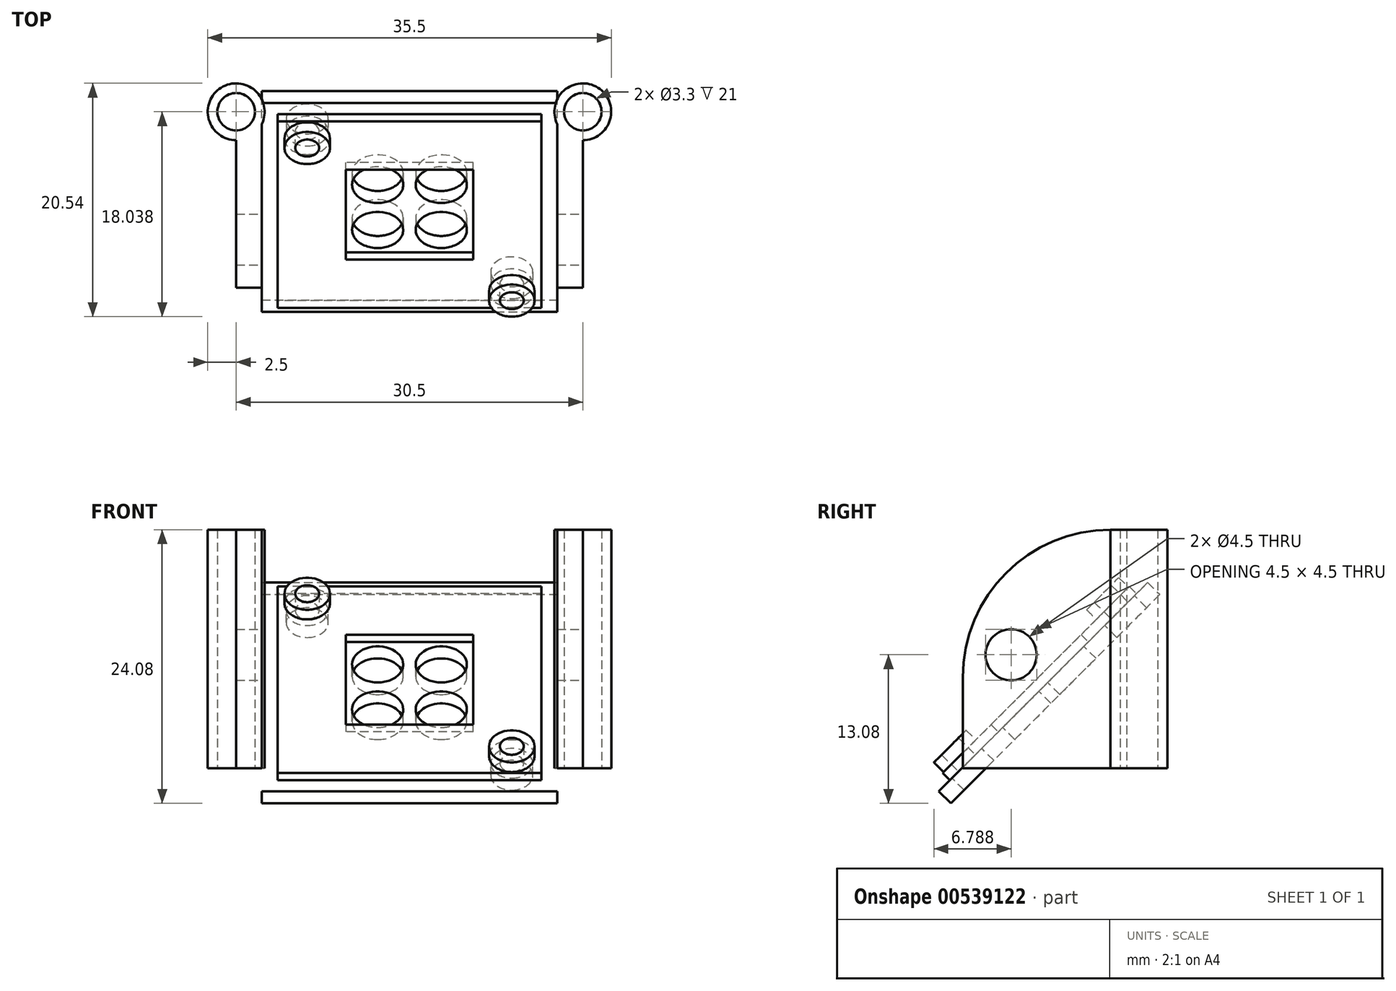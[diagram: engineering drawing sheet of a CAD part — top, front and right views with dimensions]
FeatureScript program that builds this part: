
annotation { "Feature Type Name" : "Feature", "Feature Type Description" : "" }
export const myFeature = defineFeature(function(context is Context, id is Id, definition is map)
    precondition{}
    {
        {
            var Q0;
            Q0=qCreatedBy(makeId("Top.planeOp"),FACE);
            var sketch = newSketch(context, id + "F0", { "sketchPlane" : qUnion([Q0])});
            skLineSegment(sketch, "E0", {"start": v(15.25, 24.62) * mm, "end": v(-15.25, 24.62) * mm, "construction": true});
            skCircle(sketch, "E1", {"center": v(-15.25, 24.62) * mm, "radius": 1.65 * mm});
            skCircle(sketch, "E2", {"center": v(-15.25, 24.62) * mm, "radius": 2.5 * mm});
            skCircle(sketch, "E3", {"center": v(15.25, 24.62) * mm, "radius": 1.65 * mm});
            skCircle(sketch, "E4", {"center": v(15.25, 24.62) * mm, "radius": 2.5 * mm});
            skPoint(sketch, "E5", {"position": v(-15.25, 22.12) * mm});
            skLineSegment(sketch, "E6", {"start": v(-15.25, 24.62) * mm, "end": v(-15.25, 9.12) * mm, "construction": true});
            skLineSegment(sketch, "E7", {"start": v(-15.25, 9.12) * mm, "end": v(15.25, 9.12) * mm, "construction": true});
            skLineSegment(sketch, "E8", {"start": v(15.25, 9.12) * mm, "end": v(15.25, 24.62) * mm, "construction": true});
            skLineSegment(sketch, "E9", {"start": v(15.25, 22.12) * mm, "end": v(15.25, 9.12) * mm});
            skLineSegment(sketch, "E10", {"start": v(15.25, 9.12) * mm, "end": v(13, 9.12) * mm});
            skLineSegment(sketch, "E11", {"start": v(13, 9.12) * mm, "end": v(13, 23.53) * mm});
            skLineSegment(sketch, "E12", {"start": v(-15.25, 22.12) * mm, "end": v(-15.25, 9.12) * mm});
            skLineSegment(sketch, "E13", {"start": v(-15.25, 9.12) * mm, "end": v(-13, 9.12) * mm});
            skLineSegment(sketch, "E14", {"start": v(-13, 9.12) * mm, "end": v(-13, 23.53) * mm});
            skSolve(sketch);
        }
        {
            var Q0;
            Q0=makeQuery(id+"F0.imprint","IMPRINT",FACE,{"disambiguationData":[TD([[makeQuery(id+"F0.imprint","IMPRINT",EDGE,{"derivedFrom":sQuery(id+"F0.wireOp",EDGE,"E1")}),-1.0]])]});
            var Q1;
            Q1=makeQuery(id+"F0.imprint","IMPRINT",FACE,{"disambiguationData":[TD([[makeQuery(id+"F0.imprint","IMPRINT",EDGE,{"derivedFrom":sQuery(id+"F0.wireOp",EDGE,"E3")}),-1.0]])]});
            var Q2;
            Q2=makeQuery(id+"F0.imprint","IMPRINT",FACE,{"disambiguationData":[TD([[makeQuery(id+"F0.imprint","IMPRINT",EDGE,{"derivedFrom":sQuery(id+"F0.wireOp",EDGE,"GyxC4Cwi-RMFc-qVmH-YboR-WA0SqB4U5H94")}),-1.0]])]});
            var Q3;
            Q3=makeQuery(id+"F0.imprint","IMPRINT",FACE,{"disambiguationData":[TD([[makeQuery(id+"F0.imprint","IMPRINT",EDGE,{"derivedFrom":sQuery(id+"F0.wireOp",EDGE,"82AeB47f-6y09-gEI0-IFZB-KstoD60AnrTl")}),-1.0]])]});
            var Q4;
            {var subQ0=sQuery(id+"F0.wireOp",EDGE,"E9");Q4=makeQuery(id+"F0.imprint","IMPRINT",FACE,{"disambiguationData":[TD([[makeQuery(id+"F0.imprint","IMPRINT",EDGE,{"derivedFrom":subQ0}),-1.0]])]});}
            var Q5;
            {var subQ0=sQuery(id+"F0.wireOp",EDGE,"E12");Q5=makeQuery(id+"F0.imprint","IMPRINT",FACE,{"disambiguationData":[TD([[makeQuery(id+"F0.imprint","IMPRINT",EDGE,{"derivedFrom":subQ0}),1.0]])]});}
            extrude(context, id + "F1", {"entities" : qUnion([Q0, Q1, Q2, Q3, Q4, Q5]), "depth" : 21 * mm, "offsetDistance" : 25 * mm});
        }
        {
            var Q0;
            Q0=makeQuery(id+"F1.opExtrude","CAP_EDGE",EDGE,{"disambiguationData":[OSD([sQuery(id+"F0.wireOp",EDGE,"E13")])],"isStart":false});
            var Q1;
            Q1=makeQuery(id+"F1.opExtrude","CAP_EDGE",EDGE,{"disambiguationData":[OSD([sQuery(id+"F0.wireOp",EDGE,"E10")])],"isStart":false});
            fillet(context, id + "F2", {"entities" : qUnion([Q0, Q1]), "radius" : 13 * mm, "tangentPropagation" : true, "allowEdgeOverflow" : false});
        }
        {
            var Q0;
            Q0=makeQuery(id+"F1.opExtrude","SWEPT_FACE",FACE,{"disambiguationData":[OSD([sQuery(id+"F0.wireOp",EDGE,"E9")])]});
            var sketch = newSketch(context, id + "F3", { "sketchPlane" : qUnion([Q0])});
            skLineSegment(sketch, "E15", {"start": v(9.12, 0) * mm, "end": v(13.37, 0) * mm, "construction": true});
            skLineSegment(sketch, "E16", {"start": v(13.37, 0) * mm, "end": v(13.37, 10) * mm, "construction": true});
            skCircle(sketch, "E17", {"center": v(13.37, 10) * mm, "radius": 2.25 * mm});
            skSolve(sketch);
        }
        {
            var Q0;
            Q0=sQuery(id+"F3.wireOp",VERTEX,"E17.center");
            var Q1;
            Q1=makeQuery(id+"F1.opExtrude","SWEPT_BODY",BODY,{"disambiguationData":[OSD([sQuery(id+"F0.wireOp",EDGE,"E1"),sQuery(id+"F0.wireOp",EDGE,"E2"),sQuery(id+"F0.wireOp",EDGE,"E12"),sQuery(id+"F0.wireOp",EDGE,"E13"),sQuery(id+"F0.wireOp",EDGE,"E14")])]});
            var Q2;
            Q2=makeQuery(id+"F1.opExtrude","SWEPT_BODY",BODY,{"disambiguationData":[OSD([sQuery(id+"F0.wireOp",EDGE,"E3"),sQuery(id+"F0.wireOp",EDGE,"E4"),sQuery(id+"F0.wireOp",EDGE,"E9"),sQuery(id+"F0.wireOp",EDGE,"E10"),sQuery(id+"F0.wireOp",EDGE,"E11")])]});
            hole(context, id + "F4", {"style" : HoleStyle.SIMPLE, "endStyle" : HoleEndStyle.THROUGH, "holeDiameter" : 4.5 * mm, "isTappedThrough" : true, "tappedDepth" : 12 * mm, "tapClearance" : 3, "locations" : qUnion([Q0]), "scope" : qUnion([Q1, Q2])});
        }
        {
            var Q0;
            Q0=makeQuery(id+"F1.opExtrude","SWEPT_FACE",FACE,{"disambiguationData":[OSD([sQuery(id+"F0.wireOp",EDGE,"E11")])]});
            var sketch = newSketch(context, id + "F5", { "sketchPlane" : qUnion([Q0])});
            skLineSegment(sketch, "E18", {"start": v(-13.37, 10) * mm, "end": v(-13.37, 0) * mm, "construction": true});
            skLineSegment(sketch, "E19", {"start": v(-13.37, 0) * mm, "end": v(-13.37, 10) * mm, "construction": true});
            skLineSegment(sketch, "E20", {"start": v(-13.37, 10) * mm, "end": v(-16.2, 7.17) * mm, "construction": true});
            skLineSegment(sketch, "E21", {"start": v(-16.2, 7.17) * mm, "end": v(-25.39, 16.36) * mm});
            skLineSegment(sketch, "E22", {"start": v(-25.39, 16.36) * mm, "end": v(-26.45, 15.3) * mm});
            skLineSegment(sketch, "E23", {"start": v(-26.45, 15.3) * mm, "end": v(-8.06, -3.08) * mm});
            skLineSegment(sketch, "E24", {"start": v(-8.06, -3.08) * mm, "end": v(-7, -2.02) * mm});
            skLineSegment(sketch, "E25", {"start": v(-7, -2.02) * mm, "end": v(-16.2, 7.17) * mm});
            skSolve(sketch);
        }
        {
            var Q0;
            {var subQ0=sQuery(id+"F5.wireOp",EDGE,"E25");var subQ1=sQuery(id+"F5.wireOp",EDGE,"E21");var subQ2=makeQuery(id+"F5.imprint","INTERSECT",VERTEX,{"derivedFrom":[subQ1,subQ0]});Q0=makeQuery(id+"F5.imprint","IMPRINT",FACE,{"disambiguationData":[TD([[makeQuery(id+"F5.imprint","IMPRINT",EDGE,{"disambiguationData":[TD([[subQ2,-1.0]])],"derivedFrom":subQ1}),1.0]])]});}
            var Q1;
            {var subQ0=sQuery(id+"F5.wireOp",EDGE,"E22");Q1=makeQuery(id+"F5.imprint","IMPRINT",FACE,{"disambiguationData":[TD([[makeQuery(id+"F5.imprint","IMPRINT",EDGE,{"derivedFrom":subQ0}),1.0]])]});}
            var Q2;
            {var subQ1=sQuery(id+"F5.wireOp",EDGE,"E24");Q2=makeQuery(id+"F5.imprint","IMPRINT",FACE,{"disambiguationData":[TD([[makeQuery(id+"F5.imprint","IMPRINT",EDGE,{"derivedFrom":subQ1}),1.0]])]});}
            extrude(context, id + "F6", {"entities" : qUnion([Q0, Q1, Q2]), "depth" : 26 * mm, "offsetDistance" : 25 * mm});
        }
        {
            var Q0;
            Q0=makeQuery(id+"F6.opExtrude","SWEPT_FACE",FACE,{"disambiguationData":[OSD([sQuery(id+"F5.wireOp",EDGE,"E21"),sQuery(id+"F5.wireOp",EDGE,"E25")])]});
            var sketch = newSketch(context, id + "F7", { "sketchPlane" : qUnion([Q0])});
            skLineSegment(sketch, "E26", {"start": v(-13, 29.52) * mm, "end": v(-9, 29.52) * mm, "construction": true});
            skLineSegment(sketch, "E27", {"start": v(-9, 29.52) * mm, "end": v(-9, 26.02) * mm, "construction": true});
            skLineSegment(sketch, "E28", {"start": v(13, 3.52) * mm, "end": v(9, 3.52) * mm, "construction": true});
            skLineSegment(sketch, "E29", {"start": v(9, 3.52) * mm, "end": v(9, 7.02) * mm, "construction": true});
            skPoint(sketch, "E30.endSnap0", {"position": v(0, 3.52) * mm});
            skLineSegment(sketch, "E31.bottom", {"start": v(11.6, 4.92) * mm, "end": v(-11.6, 4.92) * mm});
            skLineSegment(sketch, "E31.top", {"start": v(11.6, 28.12) * mm, "end": v(-11.6, 28.12) * mm});
            skLineSegment(sketch, "E31.left", {"start": v(11.6, 4.92) * mm, "end": v(11.6, 28.12) * mm});
            skLineSegment(sketch, "E31.right", {"start": v(-11.6, 4.92) * mm, "end": v(-11.6, 28.12) * mm});
            skPoint(sketch, "E31.middle", {"position": v(0, 16.52) * mm});
            skLineSegment(sketch, "E32.bottom", {"start": v(5.6, 10.92) * mm, "end": v(-5.6, 10.92) * mm});
            skLineSegment(sketch, "E32.top", {"start": v(5.6, 22.12) * mm, "end": v(-5.6, 22.12) * mm});
            skLineSegment(sketch, "E32.left", {"start": v(5.6, 10.92) * mm, "end": v(5.6, 22.12) * mm});
            skLineSegment(sketch, "E32.right", {"start": v(-5.6, 10.92) * mm, "end": v(-5.6, 22.12) * mm});
            skCircle(sketch, "E33", {"center": v(-9, 26.02) * mm, "radius": 1.05 * mm});
            skCircle(sketch, "E34", {"center": v(9, 7.02) * mm, "radius": 1.05 * mm});
            skCircle(sketch, "E35", {"center": v(9, 7.02) * mm, "radius": 2 * mm});
            skCircle(sketch, "E36", {"center": v(-9, 26.02) * mm, "radius": 2 * mm});
            skCircle(sketch, "E37", {"center": v(9, 7.02) * mm, "radius": 1.8 * mm, "construction": true});
            skCircle(sketch, "E38", {"center": v(-9, 26.02) * mm, "radius": 1.8 * mm, "construction": true});
            skLineSegment(sketch, "E39", {"start": v(0, 16.52) * mm, "end": v(-5.6, 16.52) * mm, "construction": true});
            skLineSegment(sketch, "E40", {"start": v(-2.8, 16.52) * mm, "end": v(-2.8, 22.12) * mm, "construction": true});
            skLineSegment(sketch, "E41", {"start": v(-2.8, 16.52) * mm, "end": v(-2.8, 10.92) * mm, "construction": true});
            skLineSegment(sketch, "E42", {"start": v(0, 16.52) * mm, "end": v(5.6, 16.52) * mm, "construction": true});
            skLineSegment(sketch, "E43", {"start": v(2.8, 16.52) * mm, "end": v(2.8, 22.12) * mm, "construction": true});
            skLineSegment(sketch, "E44", {"start": v(2.8, 16.52) * mm, "end": v(2.8, 10.92) * mm, "construction": true});
            skLineSegment(sketch, "E45", {"start": v(2.8, 13.72) * mm, "end": v(-2.8, 13.72) * mm, "construction": true});
            skLineSegment(sketch, "E46", {"start": v(-2.8, 13.72) * mm, "end": v(-2.8, 19.32) * mm, "construction": true});
            skLineSegment(sketch, "E47", {"start": v(-2.8, 19.32) * mm, "end": v(2.8, 19.32) * mm, "construction": true});
            skCircle(sketch, "E48", {"center": v(-2.8, 19.32) * mm, "radius": 2.25 * mm, "construction": true});
            skCircle(sketch, "E49", {"center": v(2.8, 19.32) * mm, "radius": 2.25 * mm, "construction": true});
            skCircle(sketch, "E50", {"center": v(2.8, 13.72) * mm, "radius": 2.25 * mm, "construction": true});
            skCircle(sketch, "E51", {"center": v(-2.8, 13.72) * mm, "radius": 2.25 * mm, "construction": true});
            skSolve(sketch);
        }
        {
            var Q0;
            Q0=sQuery(id+"F7.wireOp",VERTEX,"xRpNI7OB-sENC-NIWt-IonO-ULPQCYI2OJvv.center");
            var Q1;
            Q1=sQuery(id+"F7.wireOp",VERTEX,"aurLsu0g-ZDsF-CTWi-w7Pd-vwTeFcaxKEEF.center");
            var Q2;
            Q2=sQuery(id+"F7.wireOp",VERTEX,"E33.center");
            var Q3;
            Q3=sQuery(id+"F7.wireOp",VERTEX,"E29.end");
            var Q4;
            Q4=makeQuery(id+"F6.opExtrude","SWEPT_BODY",BODY,{"disambiguationData":[OSD([sQuery(id+"F5.wireOp",EDGE,"E21"),sQuery(id+"F5.wireOp",EDGE,"E22"),sQuery(id+"F5.wireOp",EDGE,"E23"),sQuery(id+"F5.wireOp",EDGE,"E24"),sQuery(id+"F5.wireOp",EDGE,"E25")])]});
            hole(context, id + "F8", {"style" : HoleStyle.SIMPLE, "endStyle" : HoleEndStyle.THROUGH, "holeDiameter" : 3.7 * mm, "isTappedThrough" : true, "tappedDepth" : 12 * mm, "tapClearance" : 3, "locations" : qUnion([Q0, Q1, Q2, Q3]), "scope" : qUnion([Q4])});
        }
        {
            var Q0;
            Q0=makeQuery(id+"F7.imprint","IMPRINT",FACE,{"disambiguationData":[TD([[makeQuery(id+"F7.imprint","IMPRINT",EDGE,{"derivedFrom":sQuery(id+"F7.wireOp",EDGE,"E31.bottom")}),-1.0]])]});
            extrude(context, id + "F9", {"entities" : qUnion([Q0]), "operationType" : NewBodyOperationType.ADD, "depth" : 0.9 * mm, "offsetDistance" : 25 * mm});
        }
        {
            var Q0;
            Q0=makeQuery(id+"F7.imprint","IMPRINT",FACE,{"disambiguationData":[TD([[makeQuery(id+"F7.imprint","IMPRINT",EDGE,{"derivedFrom":sQuery(id+"F7.wireOp",EDGE,"E33")}),-1.0]])]});
            var Q1;
            Q1=makeQuery(id+"F7.imprint","IMPRINT",FACE,{"disambiguationData":[TD([[makeQuery(id+"F7.imprint","IMPRINT",EDGE,{"derivedFrom":sQuery(id+"F7.wireOp",EDGE,"E34")}),-1.0]])]});
            extrude(context, id + "F10", {"entities" : qUnion([Q0, Q1]), "operationType" : NewBodyOperationType.ADD, "depth" : 2.1 * mm, "offsetDistance" : 25 * mm});
        }
        {
            var Q0;
            Q0=sQuery(id+"F7.wireOp",VERTEX,"E46.end");
            var Q1;
            Q1=sQuery(id+"F7.wireOp",VERTEX,"E47.end");
            var Q2;
            Q2=sQuery(id+"F7.wireOp",VERTEX,"E45.start");
            var Q3;
            Q3=sQuery(id+"F7.wireOp",VERTEX,"E46.start");
            var Q4;
            Q4=makeQuery(id+"F6.opExtrude","SWEPT_BODY",BODY,{"disambiguationData":[OSD([sQuery(id+"F5.wireOp",EDGE,"E21"),sQuery(id+"F5.wireOp",EDGE,"E22"),sQuery(id+"F5.wireOp",EDGE,"E23"),sQuery(id+"F5.wireOp",EDGE,"E24"),sQuery(id+"F5.wireOp",EDGE,"E25")])]});
            hole(context, id + "F11", {"style" : HoleStyle.SIMPLE, "endStyle" : HoleEndStyle.THROUGH, "holeDiameter" : 4.5 * mm, "isTappedThrough" : true, "tappedDepth" : 12 * mm, "tapClearance" : 3, "locations" : qUnion([Q0, Q1, Q2, Q3]), "scope" : qUnion([Q4])});
        }
    });
